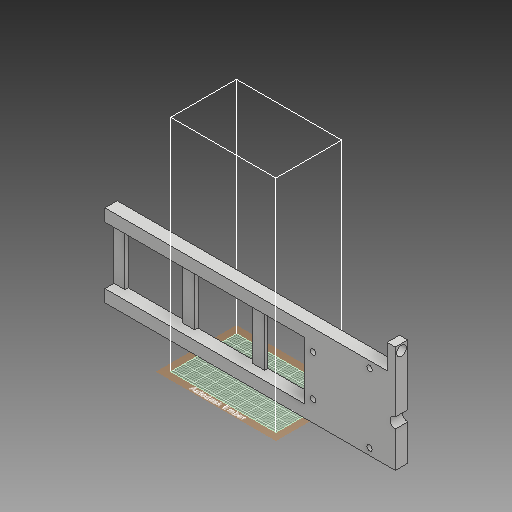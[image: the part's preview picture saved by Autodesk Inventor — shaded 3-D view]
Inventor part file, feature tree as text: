
AUTODESK INVENTOR PART (.ipt)
format: ipt  version: 2018 (Build 220112000, 112)  size: 896,512 bytes
history: native  units: mm
features: sketch x56, extrude x42, fillet x12, hole x8
ambient origin geometry x8: Origin, YZ Plane, XZ Plane, XY Plane, X Axis, Y Axis, Z Axis, Center Point
bodies: Solid1 (feature_tree)
feature tree (118):
  extrude  "Extrusion1"  Depth=50.0mm
  hole  "Hole1"  [1 undecoded]
  hole  "Hole2"  [1 undecoded]
  extrude  "Extrusion2"  Depth=2.0mm
  extrude  "Extrusion3"  Depth=2.0mm
  extrude  "Extrusion4"  Depth=5.0mm
  sketch  "Sketch7"  dims[d25=10.0mm d26=5.0mm]
  extrude  "Extrusion5"  Depth=5.0mm
  extrude  "Extrusion6"  Depth=35.0mm
  extrude  "Extrusion7"  Depth=35.0mm
  extrude  "Extrusion8"  Depth=35.0mm
  extrude  "Extrusion9"  Depth=2.0mm TaperAngle=0.0deg
  extrude  "Extrusion10"  Depth=7.5mm TaperAngle=0.0deg
  extrude  "Extrusion11"  Depth=10.0mm
  extrude  "Extrusion12"  Depth=7.5mm
  fillet  "Fillet1"  Radius=7.5mm
  fillet  "Fillet2"  Radius=25.0mm
  fillet  "Fillet3"  Radius=3.0mm
  fillet  "Fillet4"  Radius=3.2mm
  fillet  "Fillet5"  Radius=2.1mm
  fillet  "Fillet6"  Radius=5.5mm
  extrude  "Extrusion13"  Depth=92.5mm TaperAngle=0.0deg
  sketch  "Sketch17"  dims[d58=4.25mm d59=241.0mm d60=0.0mm]
  hole  "Hole3"  [1 undecoded]
  hole  "Hole4"  [1 undecoded]
  extrude  "Extrusion14"  Depth=5.0mm
  extrude  "Extrusion15"  Depth=2.5mm TaperAngle=0.0deg
  extrude  "Extrusion16"  Depth=6.35mm
  extrude  "Extrusion17"  Depth=2.5mm
  extrude  "Extrusion18"  Depth=14.55mm TaperAngle=0.0deg
  extrude  "Extrusion19"  Depth=0.1mm
  extrude  "Extrusion20"  Depth=3.25mm
  extrude  "Extrusion21"  Depth=3.25mm
  hole  "Hole5"  [1 undecoded]
  extrude  "Extrusion22"  Depth=2.0mm
  extrude  "Extrusion23"  Depth=15.0mm
  extrude  "Extrusion24"  Depth=10.0mm TaperAngle=0.0deg
  hole  "Hole6"  [1 undecoded]
  extrude  "Extrusion25"  Depth=100.0mm TaperAngle=0.0deg
  extrude  "Extrusion26"  Depth=2.0mm TaperAngle=0.0deg
  extrude  "Extrusion27"  Depth=3.3mm
  extrude  "Extrusion28"  Depth=3.3mm
  hole  "Hole7"  [1 undecoded]
  extrude  "Extrusion29"  Depth=2.0mm
  extrude  "Extrusion30"  Depth=17.0mm
  hole  "Hole8"  [1 undecoded]
  extrude  "Extrusion31"  Depth=21.0mm
  extrude  "Extrusion32"  Depth=10.0mm
  fillet  "Fillet7"  Radius=3.3mm
  fillet  "Fillet8"  Radius=10.0mm
  extrude  "Extrusion33"  Depth=5.0mm
  extrude  "Extrusion34"  Depth=5.0mm
  sketch  "Sketch45"  dims[d149=10.0mm d150=17.5mm d151=0.0mm]
  sketch  "Sketch46"  dims[d152=5.0mm]
  extrude  "Extrusion35"  Depth=10.0mm TaperAngle=0.0deg
  extrude  "Extrusion36"  Depth=2.0mm TaperAngle=0.0deg
  extrude  "Extrusion37"  Depth=3.75mm
  extrude  "Extrusion38"  Depth=3.75mm
  fillet  "Fillet9"  Radius=3.75mm
  extrude  "Extrusion39"  Depth=10.0mm TaperAngle=0.0deg
  fillet  "Fillet10"  Radius=2.0mm
  sketch  "Sketch52"  dims[d181=5.0mm d182=15.0mm d183=0.0mm]
  extrude  "Extrusion40"  Depth=15.0mm TaperAngle=0.0deg
  sketch  "Sketch54"  dims[d185=6.0mm d186=6.0mm d187=4.0mm d188=2.0mm d189=90.0deg d190=15.0mm d191=0.0mm d192=17.5mm d193=0.0mm]
  extrude  "Extrusion41"  Depth=15.0mm TaperAngle=0.0deg
  extrude  "Extrusion42"  Depth=47.5mm
  fillet  "Fillet11"  Radius=20.0mm
  fillet  "Fillet12"  Radius=5.0mm
  sketch  "Sketch1"  dims[d0=50.0mm d1=50.0mm]
  sketch  "Sketch2"  dims[d2=240.0mm d3=7.5mm]
  sketch  "Sketch3"  dims[d4=7.5mm d5=7.5mm d6=0.0mm]
  sketch  "Sketch4"  dims[d7=6.35mm d8=6.0mm d9=4.0mm d10=2.0mm d11=90.0deg d12=8.0mm d13=20.594885mm d14=25.0mm]
  sketch  "Sketch5"  dims[d15=3.3mm d16=6.0mm d17=4.0mm d18=2.0mm d19=90.0deg d20=8.0mm d21=20.594885mm d22=25.0mm]
  sketch  "Sketch6"  dims[d23=180.0deg d24=5.0mm]
  sketch  "Sketch8"  dims[d27=17.5mm d28=0.0mm d30=35.0mm]
  sketch  "Sketch9"  dims[d31=35.0mm d32=35.0mm]
  sketch  "Sketch10"  dims[d33=35.0mm d34=35.0mm]
  sketch  "Sketch11"  dims[d35=35.0mm d36=2.0mm d37=0.0mm]
  sketch  "Sketch12"  dims[d38=10.0mm d39=7.5mm d40=0.0mm]
  sketch  "Sketch13"  dims[d41=100.0mm d42=10.0mm]
  sketch  "Sketch14"  dims[d43=7.5mm d44=0.0mm d45=7.5mm d46=7.5mm d47=25.0mm d48=0.0mm d49=3.0mm d50=3.2mm d51=2.1mm d52=5.5mm]
  sketch  "Sketch15"  dims[d53=3.3mm d54=92.5mm d55=0.0mm]
  sketch  "Sketch16"  dims[d56=5.5mm d57=3.3mm]
  sketch  "Sketch18"  dims[d61=4.44mm d62=5.0mm]
  sketch  "Sketch19"  dims[d63=2.5mm d64=91.25mm d65=0.0mm]
  sketch  "Sketch20"  dims[d66=30.0mm d67=6.35mm]
  sketch  "Sketch21"  dims[d68=3.8mm d69=0.0mm d70=2.5mm]
  sketch  "Sketch22"  dims[d71=14.55mm d72=0.0mm d73=14.55mm d74=0.0mm]
  sketch  "Sketch23"  dims[d75=0.1mm d76=0.1mm]
  sketch  "Sketch24"  dims[d77=3.25mm d78=3.25mm]
  sketch  "Sketch25"  dims[d79=3.25mm d80=3.25mm]
  sketch  "Sketch26"  dims[d81=35.0mm d82=10.0mm]
  sketch  "Sketch27"  dims[d83=2.0mm d84=0.0mm d85=3.6mm]
  sketch  "Sketch28"  dims[d86=3.6mm]
  sketch  "Sketch29"  dims[d87=3.3mm d88=6.0mm d89=4.0mm d90=2.0mm d91=90.0deg d92=15.0mm d93=20.594885mm]
  sketch  "Sketch30"  dims[d94=3.3mm d95=6.0mm d96=4.0mm d97=2.0mm d98=90.0deg d99=15.0mm d100=20.594885mm d101=6.0mm]
  sketch  "Sketch31"  dims[d102=20.0mm d103=0.0mm d104=10.0mm d105=0.0mm]
  sketch  "Sketch32"  dims[d106=2.0mm d107=0.0mm d108=4.0mm]
  sketch  "Sketch33"  dims[d109=100.0mm d110=0.0mm d111=100.0mm d112=0.0mm]
  sketch  "Sketch34"  dims[d113=5.0mm d114=2.0mm d115=0.0mm]
  sketch  "Sketch35"  dims[d116=3.3mm d117=3.3mm]
  sketch  "Sketch36"  dims[d118=3.3mm d119=3.3mm]
  sketch  "Sketch37"  dims[d120=2.0mm d121=0.0mm d122=5.5mm d123=0.0mm]
  sketch  "Sketch38"  dims[d124=3.3mm d125=6.0mm d126=4.0mm d127=2.0mm d128=90.0deg d129=8.0mm d130=20.594885mm d131=42.0mm]
  sketch  "Sketch39"  dims[d132=17.0mm d133=21.0mm]
  sketch  "Sketch40"  dims[d135=8.5mm d136=15.825mm]
  sketch  "Sketch41"  dims[d137=3.5mm d138=21.0mm]
  sketch  "Sketch42"  dims[d139=3.3mm d140=3.3mm d141=3.3mm d142=10.0mm d143=0.0mm]
  sketch  "Sketch43"  dims[d144=7.5mm d145=0.0mm d146=5.0mm]
  sketch  "Sketch44"  dims[d147=10.0mm d148=5.0mm]
  sketch  "Sketch47"  dims[d153=7.0mm d154=6.0mm d155=4.0mm d156=2.0mm d157=90.0deg d158=8.0mm d159=20.594885mm d160=17.5mm d161=0.0mm]
  sketch  "Sketch48"  dims[d162=170.5mm d163=0.0mm d164=3.75mm]
  sketch  "Sketch49"  dims[d165=3.75mm d166=3.75mm d167=3.75mm]
  sketch  "Sketch50"  dims[d168=10.0mm d169=0.0mm d170=100.0mm d171=0.0mm]
  sketch  "Sketch51"  dims[d172=5.0mm d173=6.0mm d174=4.0mm d175=2.0mm d176=90.0deg d177=15.0mm d178=0.0mm d179=2.0mm d180=0.0mm]
  sketch  "Sketch53"  dims[d184=7.5mm]
  sketch  "Sketch55"  dims[d194=23.75mm d195=47.5mm d200=20.0mm d203=5.0mm]
  sketch  "Sketch56"  dims[d204=5.0mm d205=29.0mm d206=29.0mm d207=7.5mm d208=0.0mm d209=4.0mm d210=4.0mm d211=2.0mm d212=0.0mm d213=12.0mm d214=2.0mm d215=0.0mm d216=7.5mm d217=7.5mm d218=20.0mm d219=0.0mm d220=20.0mm d221=3.3mm d222=20.0mm d223=0.0mm d224=100.0mm d225=0.0mm d226=56.043mm d227=56.043mm d228=3.0mm d229=74.0mm d230=3.0mm d231=77.0mm d232=3.0mm d233=74.0mm d234=3.0mm d235=1.0mm d236=0.0mm d237=2.0mm d238=56.043mm d239=56.043mm d240=56.043mm d241=3.0mm d242=3.0mm d243=1.0mm d244=0.0mm d245=2.0mm d246=1.0mm d247=0.0mm d248=7.5mm d249=0.0mm d250=6.35mm d251=7.5mm d252=0.0mm d253=2.0mm d254=2.0mm]
note: 8 required parameter values undecoded (feature->parameter linkage not recoverable at this tier; creation-order binding heuristic only, values carry confidence <= 0.55)
